# Revit family: Lighting_Emergency&Security_Luznor_L-Basic-Led-watertight-IP67_ESP
name_source: partatom
category: Lighting Fixtures
revit_build: Autodesk Revit 2018 (Build: 20190510_1515(x64)
units: mm (PartAtom-declared; Revit-internal decimal feet)

## family parameters
Cut with Voids When Loaded = No
Host = Face
Light Source = Yes
OmniClass Number = 23.35.47.13
OmniClass Title = Emergency Lighting
Part Type = Normal
Room Calculation Point = No
Round Connector Dimension = Use Diameter
Shared = No

## types (1)
- L Basic Led watertight (IP67)
    Altura = 142 mm  [stored 0.465879 ft]
    Anchura = 288 mm  [stored 0.944882 ft]
    Apparent Load = 0 VA
    BIMobject category = Emergency & Security
    Color Filter = 16777215
    Default Elevation = 1219 mm
    Description = El nuevo concepto de alumbrado de emergencia disponible en modo no permanente y permanente. Con un amplio rango de flujos lumínicos. Caja estancaIP-67. Envolvente 100% policarbonato con difusor transparente de serie u opal fuerte (-30%). Montaje en superficie. Baterías Ni-Cd de alta temperatura.
Características
 IP-67 Envolvente 100% policarbonato con difusor transparente de serie u opal fuerte (flujo -30%) Difusor interno 100% policarbonato, transparente de serie, opcional opal suave o fuerte Tecnología LED Baterías Ni-Cd de alta temperatura Eficiencia energética
    Design country = Spain
    Dimming Lamp Color Temperature Shift = <None>
    Edition number = 1
    Emit Shape Visible in Rendering = No
    Emit from Rectangle Length = 267 mm
    Emit from Rectangle Width = 121 mm
    Especificación técnica = Color: Blanco frío (5.700 K) Flujo en emergencia (lm): 100 - 450 Flujo en presencia de red (lm): 100 - 450 Indicador de carga: 1 x LED verde Autonomía (h): 1-2-3 Fuente de alimentación: 110 Vac - 230 Vac - 50/60 Hz Telemandable: Si (TL-300) Índice de protección: IP65 - IK04 Aislamiento eléctrico: Clase II Normativa: Marcado CE (93/68/EEC): 2014/35/UE, 2014/30/UE and 2011/65/UE
    Horas de autonomía = Autonomía : 1 hora
    IFC Classification = Lamp
    Información difusor = El difusor se puede solicitar en 3 acabados diferentes: transparente (paso del 100% de la luz), opal suave (paso del 92% de la luz), u ópalo fuerte (paseo del 72% de la luz)
    Intensidad luminosa = Revisar por favor el link en la descripción técnica para comprobar las diferentes opciones ofrecidas por el fabricante
    Lamp = LED
    Manufacturer = Luznor
    Manufacturer country = Spain
    Manufacturer name = Luznor
    Masterformat 2014 Code = 26 52 00
    Masterformat 2014 Description = Emergency Lighting
    Material caja = Luznor - Plástico - Gris
    Material main = Polycarbonate
    Model = L Basic Led watertight (IP67)
    NBS Reference Code = 70-50-74
    NBS Reference Description = Self-Contained Emergency Luminaires
    OmniClass Code = 23-35 47 13
    OmniClass Description = Emergency Lighting
    Photometric Web File = LLBasicLed.IES
    Product Guid = 25f0c4d4-730a-4972-8a74-8d162172173a
    Product SKU = L-Basic-Led-IP67
    Product data url = https://bimobject.com
    Product family = L series
    Product group = L Basic Led
    Product name = L Basic Led watertight (IP67)
    Product url = https://www.luznor.com
    Profundidad = 74 mm  [stored 0.242782 ft]
    QR code = https://bimobject.com
    Tilt Angle = -90.00°
    UNSPSC Code = 391117
    URL = https://www.luznor.com
    Uniclass 1.4 Code = JV55
    Uniclass 1.4 Description = Self contained emergency and signage systems
    Uniclass 2.0 Code = PR-70-50-74
    Uniclass 2.0 Description = Self-Contained Emergency Luminaires
    Uniclass 2015 Code = Pr_70_70_48_77
    Uniclass 2015 Name = Self-contained emergency luminaires
    Uniformat II Code = D5020
    Uniformat II Description = Lighting & Branch Wiring

note: [stored X ft] marks values corroborated as IEEE doubles in the binary element streams (Revit-internal decimal feet)

## geometry (parser evidence)
native form markers: Sweep x7
no freeform markers — native parametric forms only
